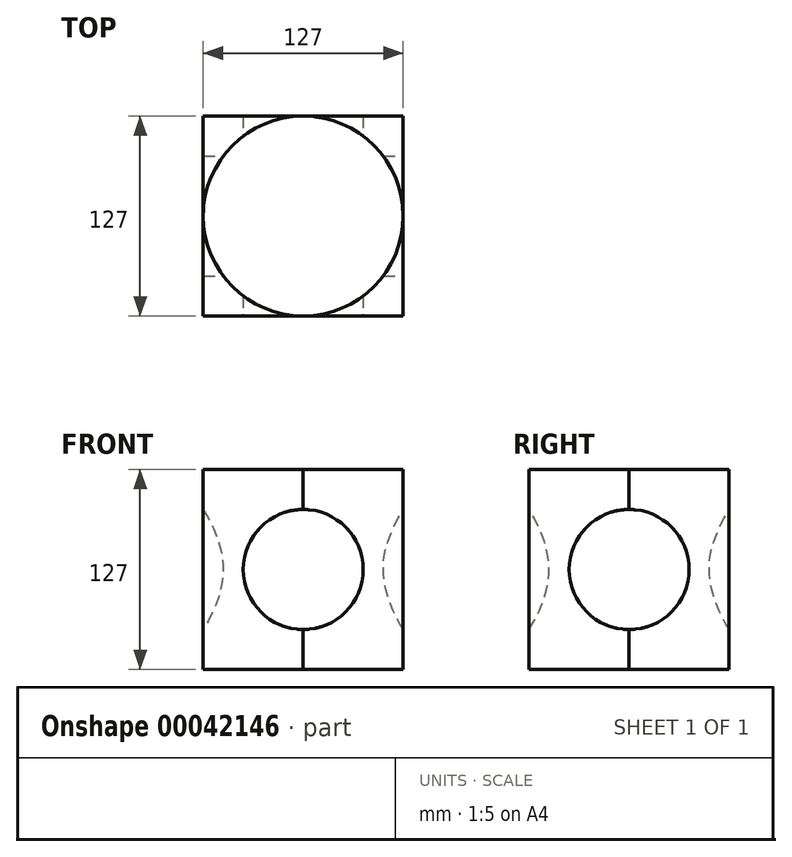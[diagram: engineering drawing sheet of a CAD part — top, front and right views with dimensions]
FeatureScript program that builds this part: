
annotation { "Feature Type Name" : "Feature", "Feature Type Description" : "" }
export const myFeature = defineFeature(function(context is Context, id is Id, definition is map)
    precondition{}
    {
        {
            var Q0;
            Q0=qCreatedBy(makeId("Front.planeOp"),FACE);
            var sketch = newSketch(context, id + "F0", { "sketchPlane" : qUnion([Q0])});
            skLineSegment(sketch, "E0", {"start": v(0, 127) * mm, "end": v(0, 0) * mm});
            skLineSegment(sketch, "E1", {"start": v(0, 0) * mm, "end": v(127, 0) * mm});
            skLineSegment(sketch, "E2", {"start": v(127, 0) * mm, "end": v(127, 127) * mm});
            skLineSegment(sketch, "E3", {"start": v(0, 127) * mm, "end": v(127, 127) * mm});
            skSolve(sketch);
        }
        {
            var Q0;
            Q0=makeQuery(id+"F0.imprint","IMPRINT",FACE,{"disambiguationData":[TD([[makeQuery(id+"F0.imprint","IMPRINT",EDGE,{"derivedFrom":sQuery(id+"F0.wireOp",EDGE,"E0")}),1.0]])]});
            extrude(context, id + "F1", {"entities" : qUnion([Q0]), "depth" : 127 * mm});
        }
        {
            var Q0;
            Q0=makeQuery(id+"F1.opExtrude","CAP_FACE",FACE,{"disambiguationData":[OSD([sQuery(id+"F0.wireOp",EDGE,"E0"),sQuery(id+"F0.wireOp",EDGE,"E1"),sQuery(id+"F0.wireOp",EDGE,"E2"),sQuery(id+"F0.wireOp",EDGE,"E3")])],"isStart":false});
            var sketch = newSketch(context, id + "F2", { "sketchPlane" : qUnion([Q0])});
            skLineSegment(sketch, "E4", {"start": v(0, 0) * mm, "end": v(127, 127) * mm});
            skLineSegment(sketch, "E5", {"start": v(0, 127) * mm, "end": v(127, 0) * mm});
            skCircle(sketch, "E6", {"center": v(63.5, 63.5) * mm, "radius": 38.1 * mm});
            skSolve(sketch);
        }
        {
            var Q0;
            Q0=makeQuery(id+"F1.opExtrude","SWEPT_FACE",FACE,{"disambiguationData":[OSD([sQuery(id+"F0.wireOp",EDGE,"E2")])]});
            var sketch = newSketch(context, id + "F3", { "sketchPlane" : qUnion([Q0])});
            skLineSegment(sketch, "E7", {"start": v(-127, 0) * mm, "end": v(0, 127) * mm});
            skLineSegment(sketch, "E8", {"start": v(-127, 127) * mm, "end": v(0, 0) * mm});
            skCircle(sketch, "E9", {"center": v(-63.5, 63.5) * mm, "radius": 38.1 * mm});
            skSolve(sketch);
        }
        {
            var Q0;
            Q0=makeQuery(id+"F1.opExtrude","SWEPT_FACE",FACE,{"disambiguationData":[OSD([sQuery(id+"F0.wireOp",EDGE,"E3")])]});
            var sketch = newSketch(context, id + "F4", { "sketchPlane" : qUnion([Q0])});
            skLineSegment(sketch, "E10", {"start": v(0, -127) * mm, "end": v(127, 0) * mm});
            skLineSegment(sketch, "E11", {"start": v(0, 0) * mm, "end": v(127, -127) * mm});
            skCircle(sketch, "E12", {"center": v(63.5, -63.5) * mm, "radius": 63.5 * mm});
            skSolve(sketch);
        }
        {
            var Q0;
            Q0 = qSketchRegion(id + "F3", true);
            extrude(context, id + "F5", {"entities" : qUnion([Q0]), "operationType" : NewBodyOperationType.REMOVE, "oppositeDirection" : true, "depth" : 127 * mm});
        }
        {
            var Q0;
            Q0 = qSketchRegion(id + "F2", true);
            extrude(context, id + "F6", {"entities" : qUnion([Q0]), "operationType" : NewBodyOperationType.REMOVE, "oppositeDirection" : true, "depth" : 127 * mm});
        }
        {
            var Q0;
            Q0 = qSketchRegion(id + "F4", true);
            extrude(context, id + "F7", {"entities" : qUnion([Q0]), "operationType" : NewBodyOperationType.REMOVE, "oppositeDirection" : true, "depth" : 127 * mm});
        }
    });
